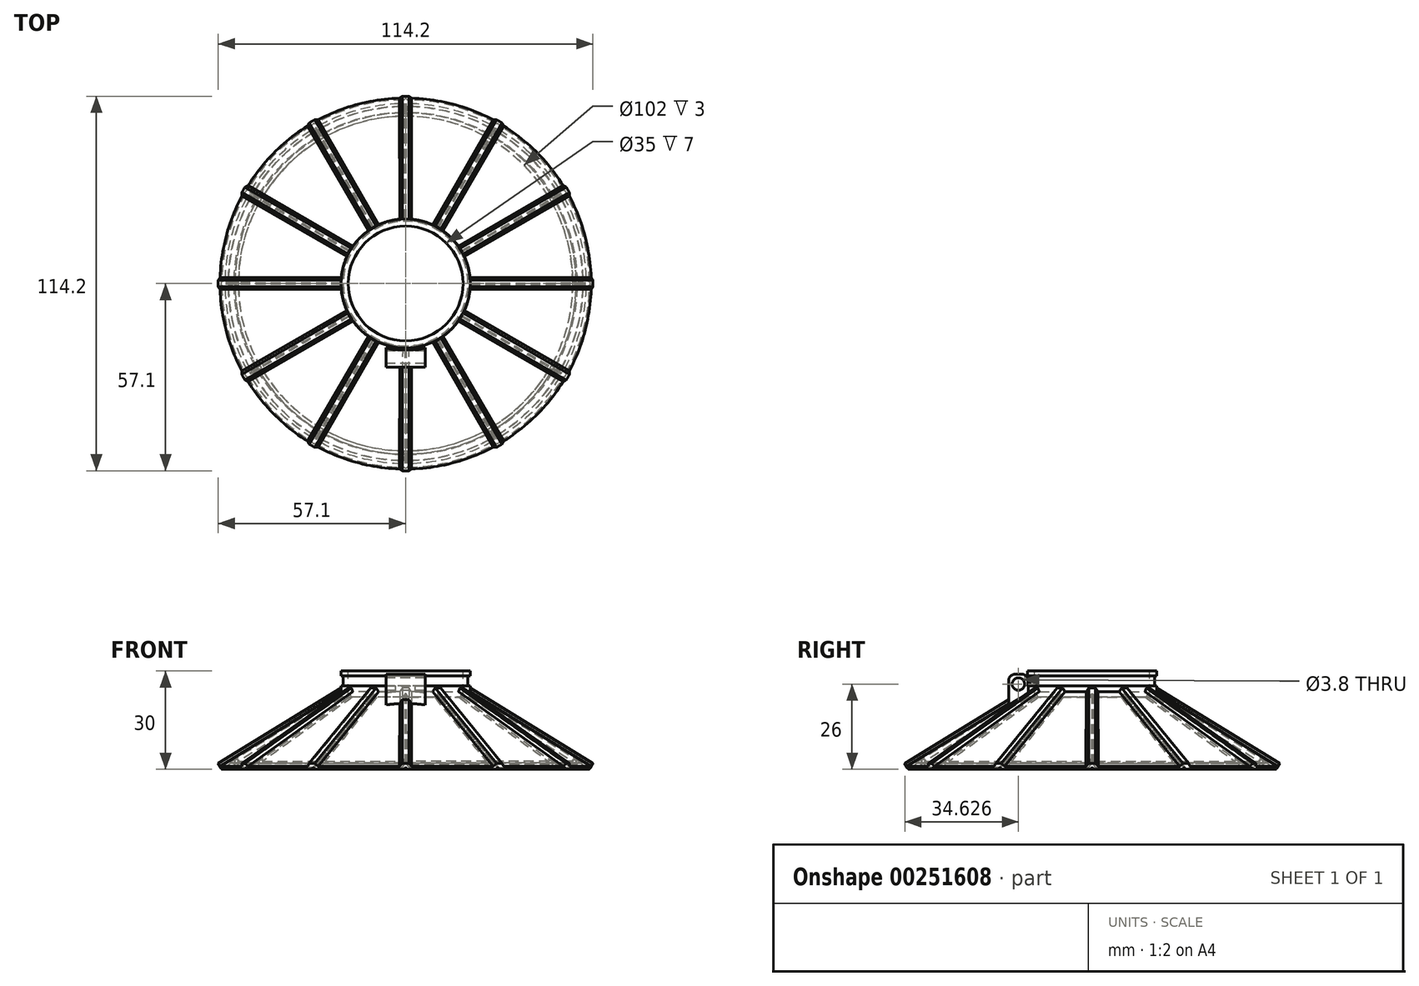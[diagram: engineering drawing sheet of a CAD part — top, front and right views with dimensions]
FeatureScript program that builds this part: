
annotation { "Feature Type Name" : "Feature", "Feature Type Description" : "" }
export const myFeature = defineFeature(function(context is Context, id is Id, definition is map)
    precondition{}
    {
        {
            var Q0;
            Q0=qCreatedBy(makeId("Top.planeOp"),FACE);
            var sketch = newSketch(context, id + "F0", { "sketchPlane" : qUnion([Q0])});
            skCircle(sketch, "E0", {"center": v(0, 0) * mm, "radius": 60 * mm, "construction": true});
            skCircle(sketch, "E1", {"center": v(0, 0) * mm, "radius": 56 * mm, "construction": true});
            skArc(sketch, "E2", {"start": v(-51.14, 27.37) * mm, "mid": v(-56.02, 15.01) * mm, "end": v(-57.97, 1.87) * mm});
            skLineSegment(sketch, "E3", {"start": v(-1.87, 57.97) * mm, "end": v(-1, 60) * mm});
            skLineSegment(sketch, "E4", {"start": v(-1, 60) * mm, "end": v(1, 60) * mm});
            skLineSegment(sketch, "E5", {"start": v(1, 60) * mm, "end": v(1.87, 57.97) * mm});
            skLineSegment(sketch, "E6.1.0", {"start": v(-30.6, 49.27) * mm, "end": v(-30.86, 51.45) * mm});
            skLineSegment(sketch, "E6.1.1", {"start": v(-29.13, 52.45) * mm, "end": v(-27.37, 51.14) * mm});
            skLineSegment(sketch, "E6.1.2", {"start": v(-30.86, 51.45) * mm, "end": v(-29.13, 52.45) * mm});
            skLineSegment(sketch, "E6.2.0", {"start": v(-51.14, 27.37) * mm, "end": v(-52.45, 29.13) * mm});
            skLineSegment(sketch, "E6.2.1", {"start": v(-51.45, 30.86) * mm, "end": v(-49.27, 30.6) * mm});
            skLineSegment(sketch, "E6.2.2", {"start": v(-52.45, 29.13) * mm, "end": v(-51.45, 30.86) * mm});
            skLineSegment(sketch, "E6.3.0", {"start": v(-57.97, -1.87) * mm, "end": v(-60, -1) * mm});
            skLineSegment(sketch, "E6.3.1", {"start": v(-60, 1) * mm, "end": v(-57.97, 1.87) * mm});
            skLineSegment(sketch, "E6.3.2", {"start": v(-60, -1) * mm, "end": v(-60, 1) * mm});
            skLineSegment(sketch, "E6.4.0", {"start": v(-49.27, -30.6) * mm, "end": v(-51.45, -30.86) * mm});
            skLineSegment(sketch, "E6.4.1", {"start": v(-52.45, -29.13) * mm, "end": v(-51.14, -27.37) * mm});
            skLineSegment(sketch, "E6.4.2", {"start": v(-51.45, -30.86) * mm, "end": v(-52.45, -29.13) * mm});
            skLineSegment(sketch, "E6.5.0", {"start": v(-27.37, -51.14) * mm, "end": v(-29.13, -52.45) * mm});
            skLineSegment(sketch, "E6.5.1", {"start": v(-30.86, -51.45) * mm, "end": v(-30.6, -49.27) * mm});
            skLineSegment(sketch, "E6.5.2", {"start": v(-29.13, -52.45) * mm, "end": v(-30.86, -51.45) * mm});
            skLineSegment(sketch, "E6.6.0", {"start": v(1.87, -57.97) * mm, "end": v(1, -60) * mm});
            skLineSegment(sketch, "E6.6.1", {"start": v(-1, -60) * mm, "end": v(-1.87, -57.97) * mm});
            skLineSegment(sketch, "E6.6.2", {"start": v(1, -60) * mm, "end": v(-1, -60) * mm});
            skLineSegment(sketch, "E6.7.0", {"start": v(30.6, -49.27) * mm, "end": v(30.86, -51.45) * mm});
            skLineSegment(sketch, "E6.7.1", {"start": v(29.13, -52.45) * mm, "end": v(27.37, -51.14) * mm});
            skLineSegment(sketch, "E6.7.2", {"start": v(30.86, -51.45) * mm, "end": v(29.13, -52.45) * mm});
            skLineSegment(sketch, "E6.8.0", {"start": v(51.14, -27.37) * mm, "end": v(52.45, -29.13) * mm});
            skLineSegment(sketch, "E6.8.1", {"start": v(51.45, -30.86) * mm, "end": v(49.27, -30.6) * mm});
            skLineSegment(sketch, "E6.8.2", {"start": v(52.45, -29.13) * mm, "end": v(51.45, -30.86) * mm});
            skLineSegment(sketch, "E6.9.0", {"start": v(57.97, 1.87) * mm, "end": v(60, 1) * mm});
            skLineSegment(sketch, "E6.9.1", {"start": v(60, -1) * mm, "end": v(57.97, -1.87) * mm});
            skLineSegment(sketch, "E6.9.2", {"start": v(60, 1) * mm, "end": v(60, -1) * mm});
            skLineSegment(sketch, "E6.10.0", {"start": v(49.27, 30.6) * mm, "end": v(51.45, 30.86) * mm});
            skLineSegment(sketch, "E6.10.1", {"start": v(52.45, 29.13) * mm, "end": v(51.14, 27.37) * mm});
            skLineSegment(sketch, "E6.10.2", {"start": v(51.45, 30.86) * mm, "end": v(52.45, 29.13) * mm});
            skLineSegment(sketch, "E6.11.0", {"start": v(27.37, 51.14) * mm, "end": v(29.13, 52.45) * mm});
            skLineSegment(sketch, "E6.11.1", {"start": v(30.86, 51.45) * mm, "end": v(30.6, 49.27) * mm});
            skLineSegment(sketch, "E6.11.2", {"start": v(29.13, 52.45) * mm, "end": v(30.86, 51.45) * mm});
            skArc(sketch, "E7.trimOffspring", {"start": v(-30.6, 49.27) * mm, "mid": v(-41.01, 41.01) * mm, "end": v(-49.27, 30.6) * mm});
            skArc(sketch, "E8.trimOffspring", {"start": v(-1.87, 57.97) * mm, "mid": v(-15.01, 56.02) * mm, "end": v(-27.37, 51.14) * mm});
            skArc(sketch, "E9.trimOffspring", {"start": v(27.37, 51.14) * mm, "mid": v(15.01, 56.02) * mm, "end": v(1.87, 57.97) * mm});
            skArc(sketch, "E10.trimOffspring", {"start": v(49.27, 30.6) * mm, "mid": v(41.01, 41.01) * mm, "end": v(30.6, 49.27) * mm});
            skArc(sketch, "E11.trimOffspring", {"start": v(57.97, 1.87) * mm, "mid": v(56.02, 15.01) * mm, "end": v(51.14, 27.37) * mm});
            skArc(sketch, "E12.trimOffspring", {"start": v(51.14, -27.37) * mm, "mid": v(56.02, -15.01) * mm, "end": v(57.97, -1.87) * mm});
            skArc(sketch, "E13.trimOffspring", {"start": v(30.6, -49.27) * mm, "mid": v(41.01, -41.01) * mm, "end": v(49.27, -30.6) * mm});
            skArc(sketch, "E14.trimOffspring", {"start": v(1.87, -57.97) * mm, "mid": v(15.01, -56.02) * mm, "end": v(27.37, -51.14) * mm});
            skArc(sketch, "E15.trimOffspring", {"start": v(-27.37, -51.14) * mm, "mid": v(-15.01, -56.02) * mm, "end": v(-1.87, -57.97) * mm});
            skArc(sketch, "E16.trimOffspring", {"start": v(-49.27, -30.6) * mm, "mid": v(-41.01, -41.01) * mm, "end": v(-30.6, -49.27) * mm});
            skArc(sketch, "E17.trimOffspring", {"start": v(-57.97, -1.87) * mm, "mid": v(-56.02, -15.01) * mm, "end": v(-51.14, -27.37) * mm});
            skPoint(sketch, "E18", {"position": v(0, 60) * mm});
            skSolve(sketch);
        }
        {
            var Q0;
            Q0=qCreatedBy(makeId("Top.planeOp"),FACE);
            cPlane(context, id + "F1", {"entities" : qUnion([Q0]), "cplaneType" : CPlaneType.OFFSET, "offset" : 25 * mm, "width" : 150 * mm, "height" : 150 * mm});
        }
        {
            var Q0;
            Q0=qCreatedBy(id+"F1.planeOp",FACE);
            var sketch = newSketch(context, id + "F2", { "sketchPlane" : qUnion([Q0])});
            skArc(sketch, "E19", {"start": v(-1.76, 17.41) * mm, "mid": v(-4.53, 16.9) * mm, "end": v(-7.18, 15.96) * mm});
            skCircle(sketch, "E20", {"center": v(0, 0) * mm, "radius": 19.5 * mm, "construction": true});
            skLineSegment(sketch, "E21", {"start": v(-1.76, 17.41) * mm, "end": v(-1, 19.47) * mm});
            skLineSegment(sketch, "E22", {"start": v(-1, 19.47) * mm, "end": v(1, 19.47) * mm});
            skLineSegment(sketch, "E23", {"start": v(1, 19.47) * mm, "end": v(1.76, 17.41) * mm});
            skLineSegment(sketch, "E24.1.0", {"start": v(-8.87, 17.37) * mm, "end": v(-7.18, 15.96) * mm});
            skLineSegment(sketch, "E24.1.1", {"start": v(-10.23, 14.2) * mm, "end": v(-10.6, 16.37) * mm});
            skLineSegment(sketch, "E24.1.2", {"start": v(-10.6, 16.37) * mm, "end": v(-8.87, 17.37) * mm});
            skLineSegment(sketch, "E24.2.0", {"start": v(-16.37, 10.6) * mm, "end": v(-14.2, 10.23) * mm});
            skLineSegment(sketch, "E24.2.1", {"start": v(-15.96, 7.18) * mm, "end": v(-17.37, 8.87) * mm});
            skLineSegment(sketch, "E24.2.2", {"start": v(-17.37, 8.87) * mm, "end": v(-16.37, 10.6) * mm});
            skLineSegment(sketch, "E24.3.0", {"start": v(-19.47, 1) * mm, "end": v(-17.41, 1.76) * mm});
            skLineSegment(sketch, "E24.3.1", {"start": v(-17.41, -1.76) * mm, "end": v(-19.47, -1) * mm});
            skLineSegment(sketch, "E24.3.2", {"start": v(-19.47, -1) * mm, "end": v(-19.47, 1) * mm});
            skLineSegment(sketch, "E24.4.0", {"start": v(-17.37, -8.87) * mm, "end": v(-15.96, -7.18) * mm});
            skLineSegment(sketch, "E24.4.1", {"start": v(-14.2, -10.23) * mm, "end": v(-16.37, -10.6) * mm});
            skLineSegment(sketch, "E24.4.2", {"start": v(-16.37, -10.6) * mm, "end": v(-17.37, -8.87) * mm});
            skLineSegment(sketch, "E24.5.0", {"start": v(-10.6, -16.37) * mm, "end": v(-10.23, -14.2) * mm});
            skLineSegment(sketch, "E24.5.1", {"start": v(-7.18, -15.96) * mm, "end": v(-8.87, -17.37) * mm});
            skLineSegment(sketch, "E24.5.2", {"start": v(-8.87, -17.37) * mm, "end": v(-10.6, -16.37) * mm});
            skLineSegment(sketch, "E24.6.0", {"start": v(-1, -19.47) * mm, "end": v(-1.76, -17.41) * mm});
            skLineSegment(sketch, "E24.6.1", {"start": v(1.76, -17.41) * mm, "end": v(1, -19.47) * mm});
            skLineSegment(sketch, "E24.6.2", {"start": v(1, -19.47) * mm, "end": v(-1, -19.47) * mm});
            skLineSegment(sketch, "E24.7.0", {"start": v(8.87, -17.37) * mm, "end": v(7.18, -15.96) * mm});
            skLineSegment(sketch, "E24.7.1", {"start": v(10.23, -14.2) * mm, "end": v(10.6, -16.37) * mm});
            skLineSegment(sketch, "E24.7.2", {"start": v(10.6, -16.37) * mm, "end": v(8.87, -17.37) * mm});
            skLineSegment(sketch, "E24.8.0", {"start": v(16.37, -10.6) * mm, "end": v(14.2, -10.23) * mm});
            skLineSegment(sketch, "E24.8.1", {"start": v(15.96, -7.18) * mm, "end": v(17.37, -8.87) * mm});
            skLineSegment(sketch, "E24.8.2", {"start": v(17.37, -8.87) * mm, "end": v(16.37, -10.6) * mm});
            skLineSegment(sketch, "E24.9.0", {"start": v(19.47, -1) * mm, "end": v(17.41, -1.76) * mm});
            skLineSegment(sketch, "E24.9.1", {"start": v(17.41, 1.76) * mm, "end": v(19.47, 1) * mm});
            skLineSegment(sketch, "E24.9.2", {"start": v(19.47, 1) * mm, "end": v(19.47, -1) * mm});
            skLineSegment(sketch, "E24.10.0", {"start": v(17.37, 8.87) * mm, "end": v(15.96, 7.18) * mm});
            skLineSegment(sketch, "E24.10.1", {"start": v(14.2, 10.23) * mm, "end": v(16.37, 10.6) * mm});
            skLineSegment(sketch, "E24.10.2", {"start": v(16.37, 10.6) * mm, "end": v(17.37, 8.87) * mm});
            skLineSegment(sketch, "E24.11.0", {"start": v(10.6, 16.37) * mm, "end": v(10.23, 14.2) * mm});
            skLineSegment(sketch, "E24.11.1", {"start": v(7.18, 15.96) * mm, "end": v(8.87, 17.37) * mm});
            skLineSegment(sketch, "E24.11.2", {"start": v(8.87, 17.37) * mm, "end": v(10.6, 16.37) * mm});
            skArc(sketch, "E25.trimOffspring", {"start": v(7.18, 15.96) * mm, "mid": v(4.53, 16.9) * mm, "end": v(1.76, 17.41) * mm});
            skArc(sketch, "E26.trimOffspring", {"start": v(14.2, 10.23) * mm, "mid": v(12.37, 12.37) * mm, "end": v(10.23, 14.2) * mm});
            skArc(sketch, "E27.trimOffspring", {"start": v(17.41, 1.76) * mm, "mid": v(16.9, 4.53) * mm, "end": v(15.96, 7.18) * mm});
            skArc(sketch, "E28.trimOffspring", {"start": v(15.96, -7.18) * mm, "mid": v(16.9, -4.53) * mm, "end": v(17.41, -1.76) * mm});
            skArc(sketch, "E29.trimOffspring", {"start": v(10.23, -14.2) * mm, "mid": v(12.37, -12.37) * mm, "end": v(14.2, -10.23) * mm});
            skArc(sketch, "E30.trimOffspring", {"start": v(1.76, -17.41) * mm, "mid": v(4.53, -16.9) * mm, "end": v(7.18, -15.96) * mm});
            skArc(sketch, "E31.trimOffspring", {"start": v(-7.18, -15.96) * mm, "mid": v(-4.53, -16.9) * mm, "end": v(-1.76, -17.41) * mm});
            skArc(sketch, "E32.trimOffspring", {"start": v(-14.2, -10.23) * mm, "mid": v(-12.37, -12.37) * mm, "end": v(-10.23, -14.2) * mm});
            skArc(sketch, "E33.trimOffspring", {"start": v(-17.41, -1.76) * mm, "mid": v(-16.9, -4.53) * mm, "end": v(-15.96, -7.18) * mm});
            skArc(sketch, "E34.trimOffspring", {"start": v(-15.96, 7.18) * mm, "mid": v(-16.9, 4.53) * mm, "end": v(-17.41, 1.76) * mm});
            skArc(sketch, "E35.trimOffspring", {"start": v(-10.23, 14.2) * mm, "mid": v(-12.37, 12.37) * mm, "end": v(-14.2, 10.23) * mm});
            skPoint(sketch, "E36", {"position": v(0, 19.47) * mm});
            skSolve(sketch);
        }
        {
            var Q0;
            Q0=makeQuery(id+"F2.imprint","IMPRINT",FACE,{"disambiguationData":[TD([[makeQuery(id+"F2.imprint","IMPRINT",EDGE,{"derivedFrom":sQuery(id+"F2.wireOp",EDGE,"E19")}),1.0]])]});
            var Q1;
            Q1=makeQuery(id+"F0.imprint","IMPRINT",FACE,{"disambiguationData":[TD([[makeQuery(id+"F0.imprint","IMPRINT",EDGE,{"derivedFrom":sQuery(id+"F0.wireOp",EDGE,"E2")}),1.0]])]});
            loft(context, id + "F3", {"sheetProfilesArray" : [{ "sheetProfileEntities" : qUnion([Q0]) }, { "sheetProfileEntities" : qUnion([Q1]) }]});
        }
        {
            var Q0;
            Q0=makeQuery(id+"F3.opLoft","CAP_FACE",FACE,{"disambiguationData":[OSD([makeQuery(id+"F0.imprint","IMPRINT",FACE,{"disambiguationData":[TD([[makeQuery(id+"F0.imprint","IMPRINT",EDGE,{"derivedFrom":sQuery(id+"F0.wireOp",EDGE,"E2")}),1.0]])]})])],"isStart":true});
            shell(context, id + "F4", {"entities" : qUnion([Q0]), "thickness" : 1.6 * mm});
        }
        {
            var Q0;
            Q0=makeQuery(id+"F3.opLoft","CAP_FACE",FACE,{"disambiguationData":[OSD([makeQuery(id+"F2.imprint","IMPRINT",FACE,{"disambiguationData":[TD([[makeQuery(id+"F2.imprint","IMPRINT",EDGE,{"derivedFrom":sQuery(id+"F2.wireOp",EDGE,"E19")}),1.0]])]})])],"isStart":true});
            extrude(context, id + "F5", {"entities" : qUnion([Q0]), "operationType" : NewBodyOperationType.REMOVE, "oppositeDirection" : true, "depth" : 2 * mm});
        }
        {
            var Q0;
            Q0=qCreatedBy(makeId("Top.planeOp"),FACE);
            cPlane(context, id + "F6", {"entities" : qUnion([Q0]), "cplaneType" : CPlaneType.OFFSET, "offset" : 4 * mm, "width" : 150 * mm, "height" : 150 * mm});
        }
        {
            var Q0;
            Q0=qCreatedBy(id+"F6.planeOp",FACE);
            var sketch = newSketch(context, id + "F7", { "sketchPlane" : qUnion([Q0])});
            skCircle(sketch, "E37", {"center": v(0, 0) * mm, "radius": 52 * mm});
            skCircle(sketch, "E38", {"center": v(0, 0) * mm, "radius": 51 * mm});
            skSolve(sketch);
        }
        {
            var Q0;
            Q0=makeQuery(id+"F7.imprint","IMPRINT",FACE,{"disambiguationData":[TD([[makeQuery(id+"F7.imprint","IMPRINT",EDGE,{"derivedFrom":sQuery(id+"F7.wireOp",EDGE,"E37")}),1.0]])]});
            var Q1;
            Q1=makeQuery(id+"F3.opLoft","CAP_FACE",FACE,{"disambiguationData":[OSD([makeQuery(id+"F0.imprint","IMPRINT",FACE,{"disambiguationData":[TD([[makeQuery(id+"F0.imprint","IMPRINT",EDGE,{"derivedFrom":sQuery(id+"F0.wireOp",EDGE,"E2")}),1.0]])]})])],"isStart":true});
            extrude(context, id + "F8", {"entities" : qUnion([Q0]), "operationType" : NewBodyOperationType.ADD, "endBound" : BoundingType.UP_TO_SURFACE, "oppositeDirection" : true, "endBoundEntityFace" : qUnion([Q1]), "depth" : 4 * mm, "hasSecondDirection" : true, "secondDirectionOppositeDirection" : true, "secondDirectionDepth" : 1 * mm});
        }
        {
            var Q0;
            Q0=qCreatedBy(id+"F1.planeOp",FACE);
            var sketch = newSketch(context, id + "F9", { "sketchPlane" : qUnion([Q0])});
            skLineSegment(sketch, "E39", {"start": v(-6, -19.47) * mm, "end": v(6, -19.47) * mm});
            skLineSegment(sketch, "E40", {"start": v(6, -19.47) * mm, "end": v(6, -25.47) * mm});
            skLineSegment(sketch, "E41", {"start": v(6, -25.47) * mm, "end": v(-6, -25.47) * mm});
            skLineSegment(sketch, "E42", {"start": v(-6, -25.47) * mm, "end": v(-6, -19.47) * mm});
            skPoint(sketch, "E43", {"position": v(0, -19.47) * mm});
            skPoint(sketch, "E44", {"position": v(0, -25.47) * mm});
            skPoint(sketch, "E45", {"position": v(-6, -22.47) * mm});
            skSolve(sketch);
        }
        {
            var Q0;
            Q0=makeQuery(id+"F9.imprint","IMPRINT",FACE,{"disambiguationData":[TD([[makeQuery(id+"F9.imprint","IMPRINT",EDGE,{"derivedFrom":sQuery(id+"F9.wireOp",EDGE,"E39")}),-1.0]])]});
            var Q1;
            Q1=makeQuery(id+"F3.opLoft","SWEPT_BODY",BODY,{"disambiguationData":[OSD([makeQuery(id+"F0.imprint","IMPRINT",FACE,{"disambiguationData":[TD([[makeQuery(id+"F0.imprint","IMPRINT",EDGE,{"derivedFrom":sQuery(id+"F0.wireOp",EDGE,"E2")}),1.0]])]}),makeQuery(id+"F2.imprint","IMPRINT",FACE,{"disambiguationData":[TD([[makeQuery(id+"F2.imprint","IMPRINT",EDGE,{"derivedFrom":sQuery(id+"F2.wireOp",EDGE,"E19")}),1.0]])]})])]});
            extrude(context, id + "F10", {"entities" : qUnion([Q0]), "operationType" : NewBodyOperationType.ADD, "endBound" : BoundingType.UP_TO_BODY, "oppositeDirection" : true, "endBoundEntityBody" : qUnion([Q1]), "depth" : 25 * mm, "hasSecondDirection" : true, "secondDirectionOppositeDirection" : false, "secondDirectionDepth" : 4 * mm});
        }
        {
            var Q0;
            Q0=makeQuery(id+"F10.opExtrude","CAP_EDGE",EDGE,{"disambiguationData":[OSD([sQuery(id+"F9.wireOp",EDGE,"E41")])],"isStart":true});
            var Q1;
            Q1=makeQuery(id+"F10.opExtrude","CAP_EDGE",EDGE,{"disambiguationData":[OSD([sQuery(id+"F9.wireOp",EDGE,"E39")])],"isStart":true});
            fillet(context, id + "F11", {"entities" : qUnion([Q0, Q1]), "radius" : 2 * mm, "tangentPropagation" : true, "allowEdgeOverflow" : false});
        }
        {
            var Q0;
            Q0=makeQuery(id+"F10.opExtrude","SWEPT_FACE",FACE,{"disambiguationData":[OSD([sQuery(id+"F9.wireOp",EDGE,"E42")])]});
            var sketch = newSketch(context, id + "F12", { "sketchPlane" : qUnion([Q0])});
            skPoint(sketch, "E46", {"position": v(22.47, 29) * mm});
            skPoint(sketch, "E47", {"position": v(22.47, 26) * mm});
            skSolve(sketch);
        }
        {
            var Q0;
            Q0=sQuery(id+"F12.wireOp",VERTEX,"E47");
            var Q1;
            Q1=makeQuery(id+"F3.opLoft","SWEPT_BODY",BODY,{"disambiguationData":[OSD([makeQuery(id+"F0.imprint","IMPRINT",FACE,{"disambiguationData":[TD([[makeQuery(id+"F0.imprint","IMPRINT",EDGE,{"derivedFrom":sQuery(id+"F0.wireOp",EDGE,"E0")}),1.0]])]}),makeQuery(id+"F2.imprint","IMPRINT",FACE,{"disambiguationData":[TD([[makeQuery(id+"F2.imprint","IMPRINT",EDGE,{"derivedFrom":sQuery(id+"F2.wireOp",EDGE,"E19")}),1.0]])]})])]});
            hole(context, id + "F13", {"style" : HoleStyle.SIMPLE, "endStyle" : HoleEndStyle.THROUGH, "standardTappedOrClearance" : lookupTablePath({ "standard" : "ANSI", "fit" : "Normal (ASME)", "size" : "#6", "type" : "Clearance" }), "standardBlindInLast" : lookupTablePath({ "fit" : "Free", "standard" : "ANSI", "size" : "#6", "type" : "Clearance" }), "holeDiameter" : 3.8 * mm, "tappedDepth" : 12 * mm, "tapClearance" : 3, "startFromSketch" : true, "locations" : qUnion([Q0]), "scope" : qUnion([Q1])});
        }
        {
            var Q0;
            Q0=qCreatedBy(id+"F1.planeOp",FACE);
            var sketch = newSketch(context, id + "F14", { "sketchPlane" : qUnion([Q0])});
            skCircle(sketch, "E48", {"center": v(0, 0) * mm, "radius": 19.7 * mm});
            skCircle(sketch, "E49", {"center": v(0, 0) * mm, "radius": 17.5 * mm});
            skSolve(sketch);
        }
        {
            var Q0;
            Q0=makeQuery(id+"F14.imprint","IMPRINT",FACE,{"disambiguationData":[TD([[makeQuery(id+"F14.imprint","IMPRINT",EDGE,{"derivedFrom":sQuery(id+"F14.wireOp",EDGE,"E48")}),1.0]])]});
            extrude(context, id + "F15", {"entities" : qUnion([Q0]), "operationType" : NewBodyOperationType.ADD, "oppositeDirection" : true, "depth" : 3 * mm, "hasSecondDirection" : true, "secondDirectionOppositeDirection" : false, "secondDirectionDepth" : 5 * mm});
        }
        {
            var Q0;
            Q0=makeQuery(id+"F15.opExtrude","CAP_EDGE",EDGE,{"disambiguationData":[OSD([sQuery(id+"F14.wireOp",EDGE,"E49")])],"isStart":false});
            fillet(context, id + "F16", {"entities" : qUnion([Q0]), "radius" : 1 * mm, "tangentPropagation" : true, "allowEdgeOverflow" : false});
        }
        {
            var Q0;
            Q0=qCreatedBy(makeId("Right.planeOp"),FACE);
            var sketch = newSketch(context, id + "F17", { "sketchPlane" : qUnion([Q0])});
            skLineSegment(sketch, "E50", {"start": v(-56, 0) * mm, "end": v(-58.1, 3.4) * mm});
            skLineSegment(sketch, "E51", {"start": v(-58.1, 3.4) * mm, "end": v(-60.2, 0) * mm});
            skLineSegment(sketch, "E52", {"start": v(-60.2, 0) * mm, "end": v(-56, 0) * mm});
            skLineSegment(sketch, "E53", {"start": v(-52, 0) * mm, "end": v(-54, 0) * mm});
            skLineSegment(sketch, "E54", {"start": v(-54, 0) * mm, "end": v(-54, 1) * mm});
            skLineSegment(sketch, "E55", {"start": v(-52, 1) * mm, "end": v(-52, 0) * mm});
            skArc(sketch, "E56", {"start": v(-52, 1) * mm, "mid": v(-53, 2) * mm, "end": v(-54, 1) * mm});
            skLineSegment(sketch, "E57", {"start": v(20.5, 28.5) * mm, "end": v(19, 28.5) * mm});
            skLineSegment(sketch, "E58", {"start": v(19, 28.5) * mm, "end": v(19, 25.5) * mm});
            skLineSegment(sketch, "E59", {"start": v(19, 25.5) * mm, "end": v(20.5, 25.5) * mm});
            skLineSegment(sketch, "E60", {"start": v(20.5, 25.5) * mm, "end": v(20.5, 28.5) * mm});
            skSolve(sketch);
        }
        {
            var Q0;
            Q0=makeQuery(id+"F17.imprint","IMPRINT",FACE,{"disambiguationData":[TD([[makeQuery(id+"F17.imprint","IMPRINT",EDGE,{"derivedFrom":sQuery(id+"F17.wireOp",EDGE,"E50")}),1.0]])]});
            var Q1;
            Q1=makeQuery(id+"F17.imprint","IMPRINT",FACE,{"disambiguationData":[TD([[makeQuery(id+"F17.imprint","IMPRINT",EDGE,{"derivedFrom":sQuery(id+"F17.wireOp",EDGE,"E53")}),-1.0]])]});
            var Q2;
            Q2=makeQuery(id+"F17.imprint","IMPRINT",FACE,{"disambiguationData":[TD([[makeQuery(id+"F17.imprint","IMPRINT",EDGE,{"derivedFrom":sQuery(id+"F17.wireOp",EDGE,"E57")}),1.0]])]});
            var Q3;
            Q3=makeQuery(id+"F15.opExtrude","CAP_EDGE",EDGE,{"disambiguationData":[OSD([sQuery(id+"F14.wireOp",EDGE,"E48")])],"isStart":true});
            revolve(context, id + "F18", {"operationType" : NewBodyOperationType.REMOVE, "entities" : qUnion([Q0, Q1, Q2]), "axis" : qUnion([Q3]), "revolveType" : RevolveType.FULL, "oppositeDirection" : true});
        }
    });
